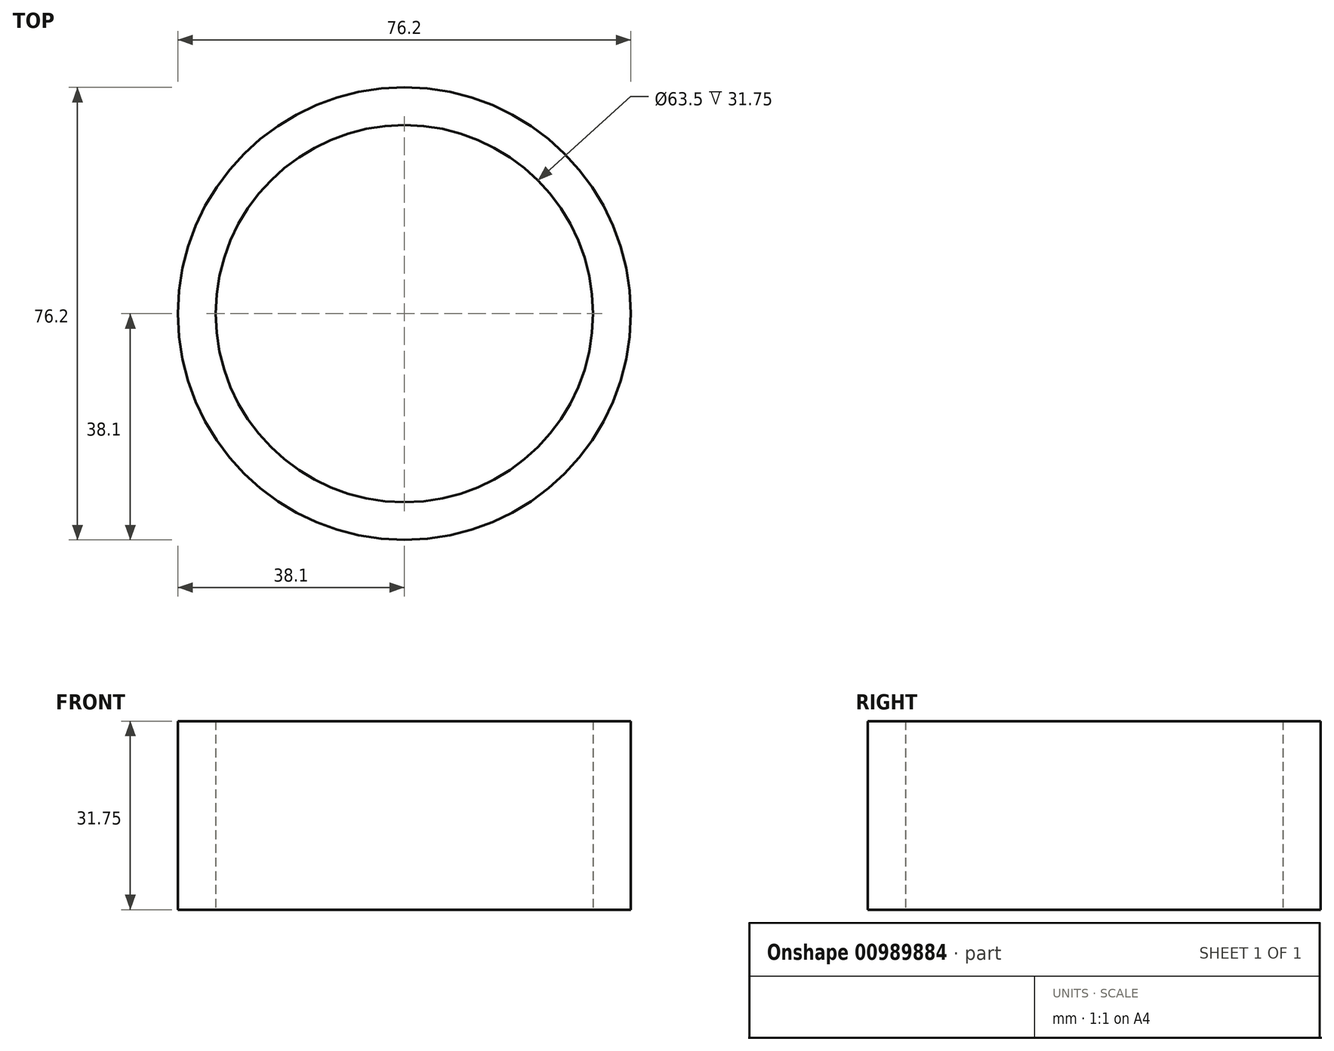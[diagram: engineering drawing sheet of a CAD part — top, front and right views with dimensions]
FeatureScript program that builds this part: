
annotation { "Feature Type Name" : "Feature", "Feature Type Description" : "" }
export const myFeature = defineFeature(function(context is Context, id is Id, definition is map)
    precondition{}
    {
        {
            var Q0;
            Q0=qCreatedBy(makeId("Top.planeOp"),FACE);
            var sketch = newSketch(context, id + "F0", { "sketchPlane" : qUnion([Q0])});
            skCircle(sketch, "E0", {"center": v(0, 0) * mm, "radius": 38.1 * mm});
            skCircle(sketch, "E1", {"center": v(0, 0) * mm, "radius": 31.75 * mm});
            skLineSegment(sketch, "E2", {"start": v(0, 0) * mm, "end": v(31.25, 5.62) * mm, "construction": true});
            skLineSegment(sketch, "E3", {"start": v(31.25, 5.62) * mm, "end": v(29.5, -11.74) * mm, "construction": true});
            skLineSegment(sketch, "E4", {"start": v(29.5, -11.74) * mm, "end": v(0, 0) * mm, "construction": true});
            skSolve(sketch);
        }
        {
            var Q0;
            Q0=makeQuery(id+"F0.imprint","IMPRINT",FACE,{"disambiguationData":[TD([[makeQuery(id+"F0.imprint","IMPRINT",EDGE,{"derivedFrom":sQuery(id+"F0.wireOp",EDGE,"E0")}),1.0]])]});
            extrude(context, id + "F1", {"entities" : qUnion([Q0]), "depth" : 6.35 * mm, "offsetDistance" : 25.4 * mm});
        }
        {
            var Q0;
            Q0=makeQuery(id+"F1.opExtrude","CAP_FACE",FACE,{"disambiguationData":[OSD([sQuery(id+"F0.wireOp",EDGE,"E0"),sQuery(id+"F0.wireOp",EDGE,"E1")])],"isStart":false});
            extrude(context, id + "F2", {"entities" : qUnion([Q0]), "operationType" : NewBodyOperationType.ADD, "depth" : 25.4 * mm, "offsetDistance" : 25.4 * mm});
        }
    });
